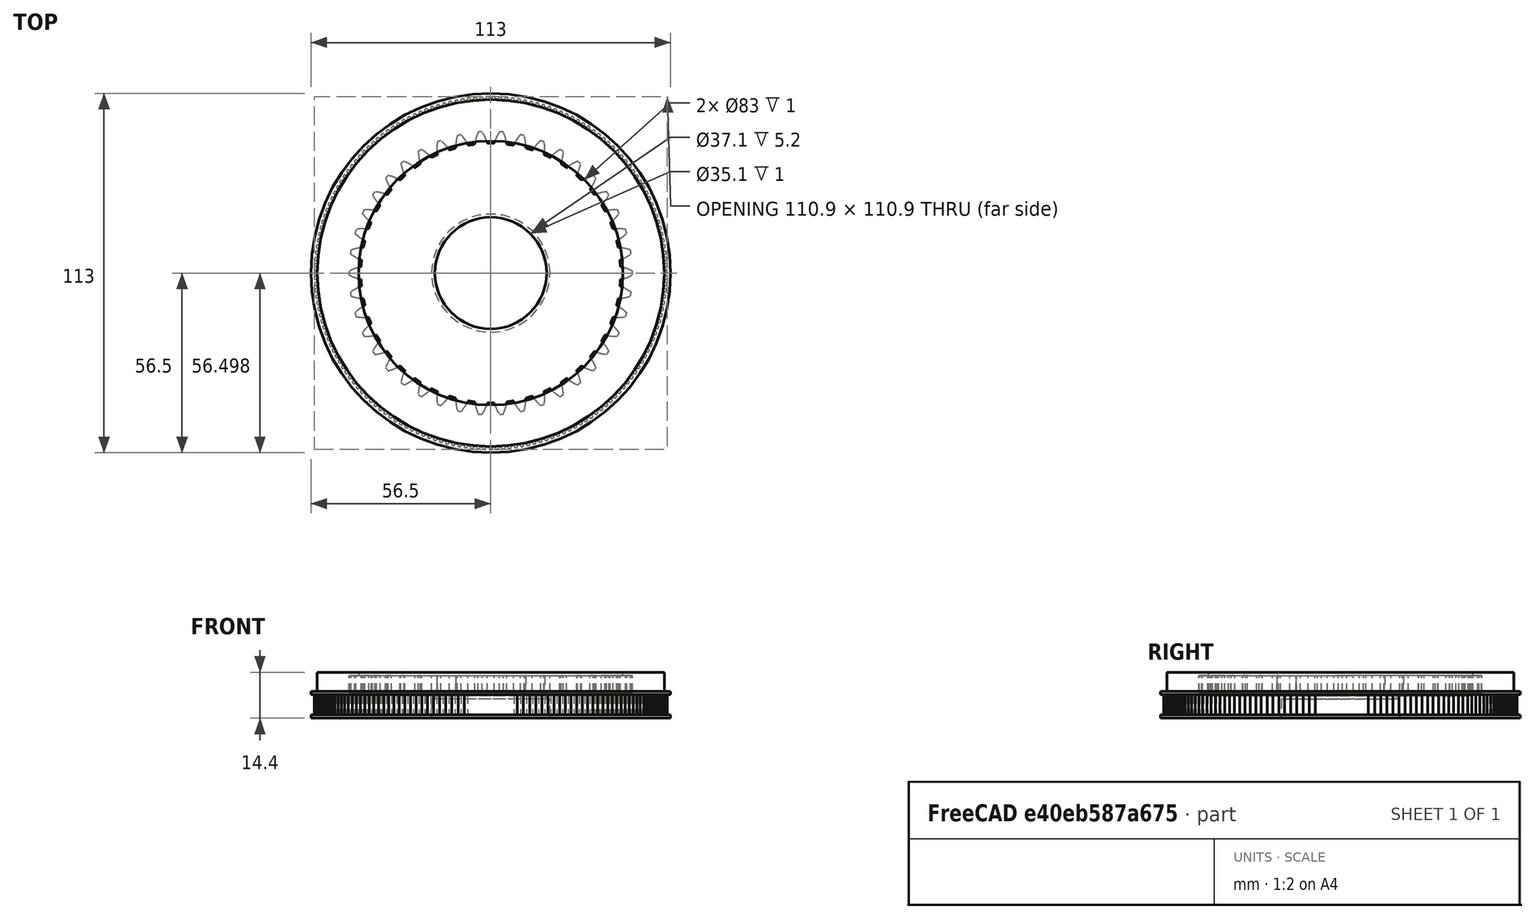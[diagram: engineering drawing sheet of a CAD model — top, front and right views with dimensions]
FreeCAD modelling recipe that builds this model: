
FCSTD DOCUMENT  (FreeCAD 0.21R33694 (Git))
Label: ring_gear
License: All rights reserved
LicenseURL: http://en.wikipedia.org/wiki/All_rights_reserved
objects: Part::Cylinder×8, Part::Cut×5, Spreadsheet::Sheet×2, Part::FeaturePython×2, Part::MultiFuse×2, Part::Fillet×1
note: 18 computed .brp shape members not serialized (recipe doc carries the construction recipe); baked Part::Feature solids carry a one-line shape summary decoded from their .brp

FEATURE [Spreadsheet::Sheet] Spreadsheet  label="settings"
  cells = A1='General settings; C1='Bearing setting; D1='mm; E1='Gearing settings; H1='Timing belt settings; I1='mm; A2='Wall thickness; B2(wall_T)=5; C2='Bearing diameter; D2(bearing_dia)=37.1; E2='Gear thickness; F2(gear_T)=5.4; H2='timing belt thickness; I2(timing_T)=6.4; C3='Bearing thickness; D3(bearing_T)=6; E3='Gear lip length; F3(gear_lips_L)=3; H3='timing lips length; I3(timing_lips_L)=2; C4='Bearing lip diameter; D4(bearing_lip_dia)=1; E4='Gear lips thickness; F4(gear_lips_T)=1; H4='timing lips thickness; I4(timing_lips_T)=1; C5='Bearing lip thickness; D5(bearing_lip_T)=1; E5='Teeth size (module); F5(gear_teeth_size)=2; E6='Planet count; F6(planet_count)=3; E7='Backlash; F7(gear_backlash)=0.2; G7='Planet divisors; E8='Ring teeth count; F8(gear_ring_teeth_cnt)=42; G8==gear_ring_teeth_cnt / planet_count; E9='Planet teeth count; F9(gear_planet_teeth_cnt)=12; G9==gear_planet_teeth_cnt / planet_count; E10='Sun teeth count; F10(gear_sun_teeth_cnt)=12; G10==gear_sun_teeth_cnt / planet_count; E11='Sun to ring ratio; F11==gear_ring_teeth_cnt / gear_sun_teeth_cnt; E12='Sun to planet ratio; F12==gear_planet_teeth_cnt / gear_sun_teeth_cnt
FEATURE [Spreadsheet::Sheet] Spreadsheet001  label="calculations"
  cells = A1='Totals; C1='Gear stuff; E1='Timing gear stuff; F1='teeth; A2='Total ring gear radius; B2(rad_ring_tot)==ring_gear_root_dia / 2 + <<settings>>.wall_T * 2; C2='ring gear reference diameter; D2(ring_gear_ref_dia)==<<settings>>.gear_teeth_size * <<settings>>.gear_ring_teeth_cnt; E2='Computed teeth; F2(timing_teeth_cnt)==ceil(2 * pi * rad_ring_tot / 2) + timing_teeth_offset_cnt; A3='Total bearing thickness; B3(total_bearing_thickness)==<<settings>>.bearing_T + <<settings>>.bearing_lip_T; C3='ring gear root diameter; D3(ring_gear_root_dia)==ring_gear_ref_dia + 2.5 * <<settings>>.gear_teeth_size; E3='teeth offset; F3(timing_teeth_offset_cnt)=3; A4='Total body thickness; B4(total_T)==<<settings>>.bearing_T + <<settings>>.bearing_lip_T + <<settings>>.gear_T + <<settings>>.gear_lips_T * 2; A6='Cilinder stackup calculations; A7='Depth Positions; C7='Cilinder Radiuses; A8='Bearing; B8(pos_bearing)=0; C8='Bearing radius; D8(rad_bearing)==<<settings>>.bearing_dia / 2; A9='Bearing lip; B9(pos_bearing_lip)==<<settings>>.bearing_T; C9='Bearing lip radius; D9(rad_bearing_lip)==<<settings>>.bearing_dia / 2 - <<settings>>.bearing_lip_dia; A10='gear bottom lip; B10(pos_gear_lip_bot)==<<settings>>.bearing_T + <<settings>>.bearing_lip_T; C10='gear bottom lip radius; D10(rad_gear_lip_bot)==ring_gear_root_dia / 2 - <<settings>>.gear_lips_L; A11='gear; B11(pos_gear)==<<settings>>.bearing_T + <<settings>>.bearing_lip_T + <<settings>>.gear_lips_T; C11='gear radius; D11(rad_gear)==ring_gear_root_dia / 2 + 1; A12='gear top lip; B12(pos_gear_lip_top)==<<settings>>.bearing_T + <<settings>>.bearing_lip_T + <<settings>>.gear_lips_T + <<settings>>.gear_T; C12='gear top lip radius; D12(rad_gear_lip_top)==ring_gear_root_dia / 2 - <<settings>>.gear_lips_L; A13='timing bottom lip position; B13(pos_timing_lip_bot)=0; C13='timing bottom lip radius; D13(rad_timing_lip_bot)==rad_ring_tot + <<settings>>.timing_lips_L; A14='timing gear position; B14(pos_timing_gear)==<<settings>>.timing_lips_T; C14='timing gear radius; D14(rad_timing_gear)==rad_ring_tot; A15='timing top position; B15(pos_timing_lip_top)==<<settings>>.timing_lips_T + <<settings>>.timing_T; C15='timing top lip radius; D15(rad_timing_lip_top)==rad_ring_tot + <<settings>>.timing_lips_L
FEATURE [Part::Cylinder] Cylinder  label="main_body"
  Angle = 360
  AttacherType = Attacher::AttachEngine3D
  FirstAngle = 0
  Height = 14.4
  Radius = 54.5
  SecondAngle = 0
  expr: Height = <<calculations>>.total_T
  expr: Radius = Spreadsheet001.rad_ring_tot
FEATURE [Part::Cylinder] Cylinder001  label="bearing_cutout"
  Angle = 360
  AttacherType = Attacher::AttachEngine3D
  FirstAngle = 0
  Height = 6
  Radius = 18.55
  SecondAngle = 0
  expr: Height = <<settings>>.bearing_T
  expr: Radius = Spreadsheet001.rad_bearing
FEATURE [Part::Cylinder] Cylinder002  label="bearing_lip_cutout"
  Angle = 360
  AttacherType = Attacher::AttachEngine3D
  FirstAngle = 0
  Height = 1
  Placement = pos=(0,0,6) rot=(0,0,1;0rad)
  Radius = 17.55
  SecondAngle = 0
  expr: .Placement.Base.z = <<calculations>>.pos_bearing_lip
  expr: Height = <<settings>>.bearing_lip_T
  expr: Radius = Spreadsheet001.rad_bearing_lip
FEATURE [Part::Cylinder] Cylinder003  label="gear_lower_lip_cutout"
  Angle = 360
  AttacherType = Attacher::AttachEngine3D
  FirstAngle = 0
  Height = 1
  Placement = pos=(0,0,7) rot=(0,0,1;0rad)
  Radius = 41.5
  SecondAngle = 0
  expr: .Placement.Base.z = Spreadsheet001.pos_gear_lip_bot
  expr: Height = <<settings>>.gear_lips_T
  expr: Radius = <<calculations>>.rad_gear_lip_bot
FEATURE [Part::Cylinder] Cylinder004  label="gear_cutout"
  Angle = 360
  AttacherType = Attacher::AttachEngine3D
  FirstAngle = 0
  Height = 5.4
  Placement = pos=(0,0,8) rot=(0,0,1;0rad)
  Radius = 45.5
  SecondAngle = 0
  expr: .Placement.Base.z = <<calculations>>.pos_gear
  expr: Height = <<settings>>.gear_T
  expr: Radius = Spreadsheet001.rad_gear
FEATURE [Part::Cylinder] Cylinder005  label="gear_upper_lip_cutout"
  Angle = 360
  AttacherType = Attacher::AttachEngine3D
  FirstAngle = 0
  Height = 1
  Placement = pos=(0,0,13.4) rot=(0,0,1;0rad)
  Radius = 41.5
  SecondAngle = 0
  expr: .Placement.Base.z = Spreadsheet001.pos_gear_lip_top
  expr: Height = <<settings>>.gear_lips_T
  expr: Radius = Spreadsheet001.rad_gear_lip_top
FEATURE [Part::FeaturePython] InternalInvoluteGear  # WARN: FeaturePython — macro-defined, semantics opaque (R4)
  AttacherType = Attacher::AttachEngine3D
  Placement = pos=(0,0,8) rot=(0,0,1;0rad)
  angular_backlash = 0.272837
  backlash = 0.2
  beta = 0
  clearance = 0.25
  da = 81.6
  df = 89
  double_helix = false
  dw = 84
  head = -0.4
  head_fillet = 0
  height = 5.4
  module = 2
  numpoints = 6
  outside_diameter = 94
  pressure_angle = 20
  properties_from_tool = false
  reversed_backlash = false
  root_fillet = 0
  shift = 0
  simple = false
  teeth = 42
  thickness = 5
  transverse_pitch = 6.28319
  version = 0.0.4
  expr: .Placement.Base.z = <<calculations>>.pos_gear
  expr: angular_backlash = backlash / dw * 360 ° / pi
  expr: backlash = <<settings>>.gear_backlash
  expr: height = <<settings>>.gear_T
  expr: module = <<settings>>.gear_teeth_size
  expr: teeth = <<settings>>.gear_ring_teeth_cnt
  expr: thickness = <<settings>>.wall_T
FEATURE [Part::FeaturePython] TimingGear  # WARN: FeaturePython — macro-defined, semantics opaque (R4)
  AttacherType = Attacher::AttachEngine3D
  Placement = pos=(0,0,1) rot=(0,0,1;0rad)
  h = 0.75
  height = 6.4
  offset = 0.4
  pitch = 2
  r0 = 0.555
  r1 = 1
  rs = 0.15
  teeth = 175
  type = 0
  u = 0.254
  version = 0.0.4
  expr: .Placement.Base.z = <<calculations>>.pos_timing_gear
  expr: height = <<settings>>.timing_T
  expr: teeth = <<calculations>>.timing_teeth_cnt
FEATURE [Part::Cylinder] Cylinder006  label="timing_lip_bot_body"
  Angle = 360
  AttacherType = Attacher::AttachEngine3D
  FirstAngle = 0
  Height = 1
  Radius = 56.5
  SecondAngle = 0
  expr: Height = <<settings>>.timing_lips_T
  expr: Radius = <<calculations>>.rad_timing_lip_bot
FEATURE [Part::Cylinder] Cylinder007  label="timing_lip_top_body"
  Angle = 360
  AttacherType = Attacher::AttachEngine3D
  FirstAngle = 0
  Height = 1
  Placement = pos=(0,0,7.4) rot=(0,0,1;0rad)
  Radius = 56.5
  SecondAngle = 0
  expr: .Placement.Base.z = <<calculations>>.pos_timing_lip_top
  expr: Height = <<settings>>.timing_lips_T
  expr: Radius = <<calculations>>.rad_timing_lip_top
FEATURE [Part::MultiFuse] Fusion
  Shapes = -> [Cylinder007,Cylinder006,TimingGear,Cylinder]
FEATURE [Part::Cut] Cut
  Base = -> Fusion
  Tool = -> Cylinder001
FEATURE [Part::Cut] Cut001
  Base = -> Cut
  Tool = -> Cylinder002
FEATURE [Part::Cut] Cut002
  Base = -> Cut001
  Tool = -> Cylinder003
FEATURE [Part::Cut] Cut003
  Base = -> Cut002
  Tool = -> Cylinder004
FEATURE [Part::Cut] Cut004
  Base = -> Cut003
  Tool = -> Cylinder005
FEATURE [Part::MultiFuse] Fusion001  label="ring_gear"
  Shapes = -> [Cut004,InternalInvoluteGear]
FEATURE [Part::Fillet] Fillet  label="bearing_insert_fillet"
  Base = -> Fusion001
  Edges = 1 edges r=0.8: [Edge853]
